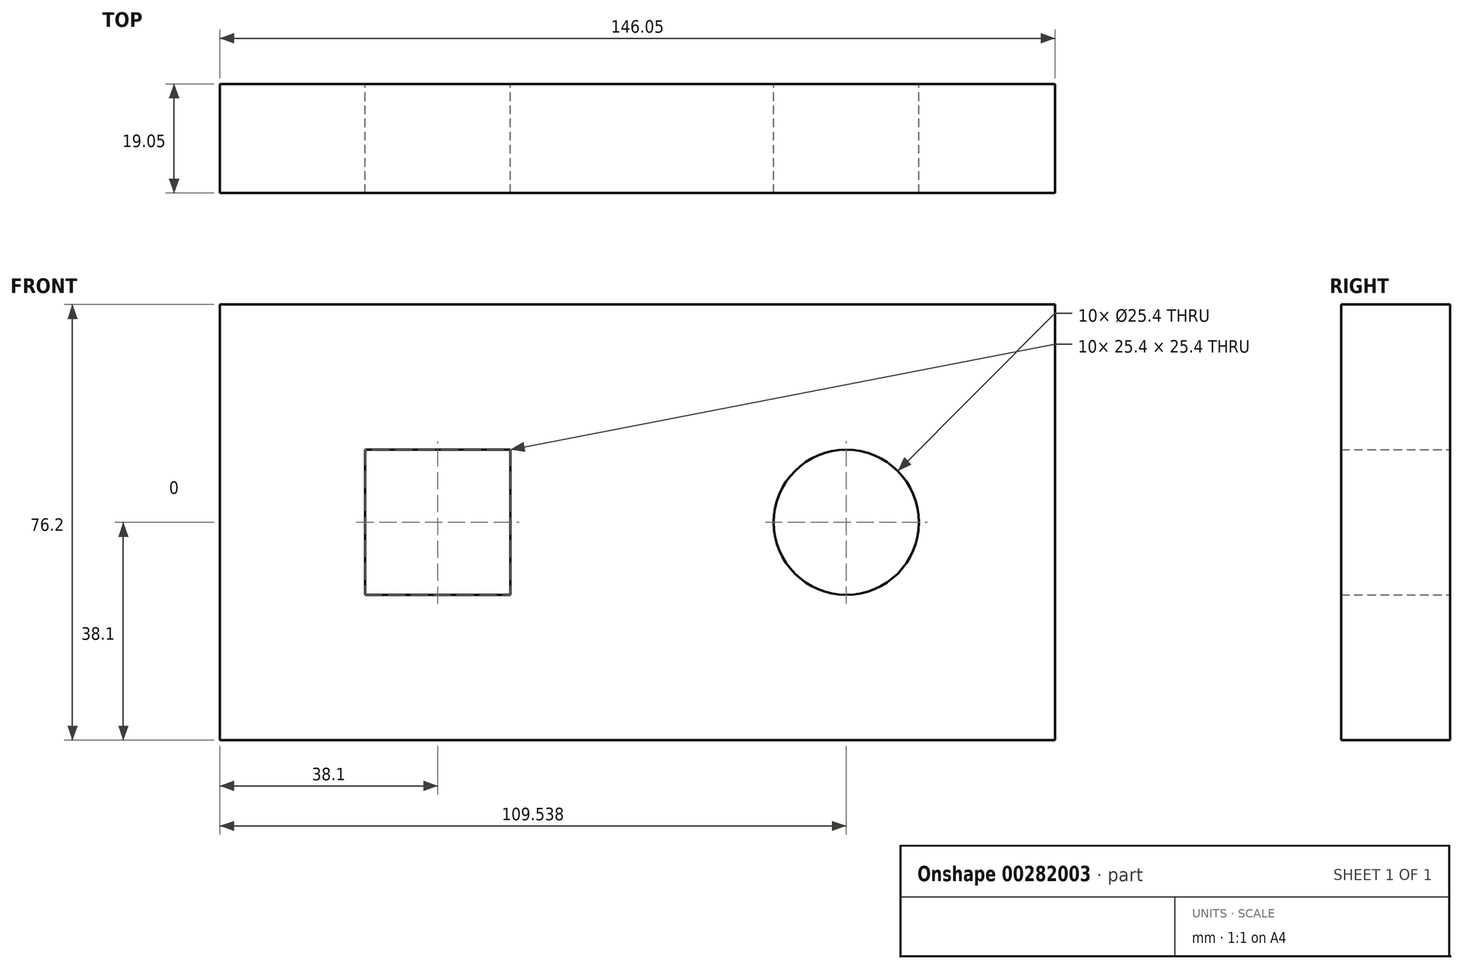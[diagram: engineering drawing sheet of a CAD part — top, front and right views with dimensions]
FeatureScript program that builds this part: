
annotation { "Feature Type Name" : "Feature", "Feature Type Description" : "" }
export const myFeature = defineFeature(function(context is Context, id is Id, definition is map)
    precondition{}
    {
        {
            var Q0;
            Q0=qCreatedBy(makeId("Front.planeOp"),FACE);
            var sketch = newSketch(context, id + "F0", { "sketchPlane" : qUnion([Q0])});
            skLineSegment(sketch, "E0.bottom", {"start": v(0, 0) * mm, "end": v(-146.05, 0) * mm});
            skLineSegment(sketch, "E0.top", {"start": v(0, 76.2) * mm, "end": v(-146.05, 76.2) * mm});
            skLineSegment(sketch, "E0.left", {"start": v(0, 0) * mm, "end": v(0, 76.2) * mm});
            skLineSegment(sketch, "E0.right", {"start": v(-146.05, 0) * mm, "end": v(-146.05, 76.2) * mm});
            skLineSegment(sketch, "E1.bottom", {"start": v(-95.25, 25.4) * mm, "end": v(-120.65, 25.4) * mm});
            skLineSegment(sketch, "E1.top", {"start": v(-95.25, 50.8) * mm, "end": v(-120.65, 50.8) * mm});
            skLineSegment(sketch, "E1.left", {"start": v(-95.25, 25.4) * mm, "end": v(-95.25, 50.8) * mm});
            skLineSegment(sketch, "E1.right", {"start": v(-120.65, 25.4) * mm, "end": v(-120.65, 50.8) * mm});
            skCircle(sketch, "E2", {"center": v(-36.51, 38.1) * mm, "radius": 12.7 * mm});
            skSolve(sketch);
        }
        {
            var Q0;
            Q0 = qSketchRegion(id + "F0", true);
            extrude(context, id + "F1", {"entities" : qUnion([Q0]), "depth" : 19.05 * mm});
        }
    });
